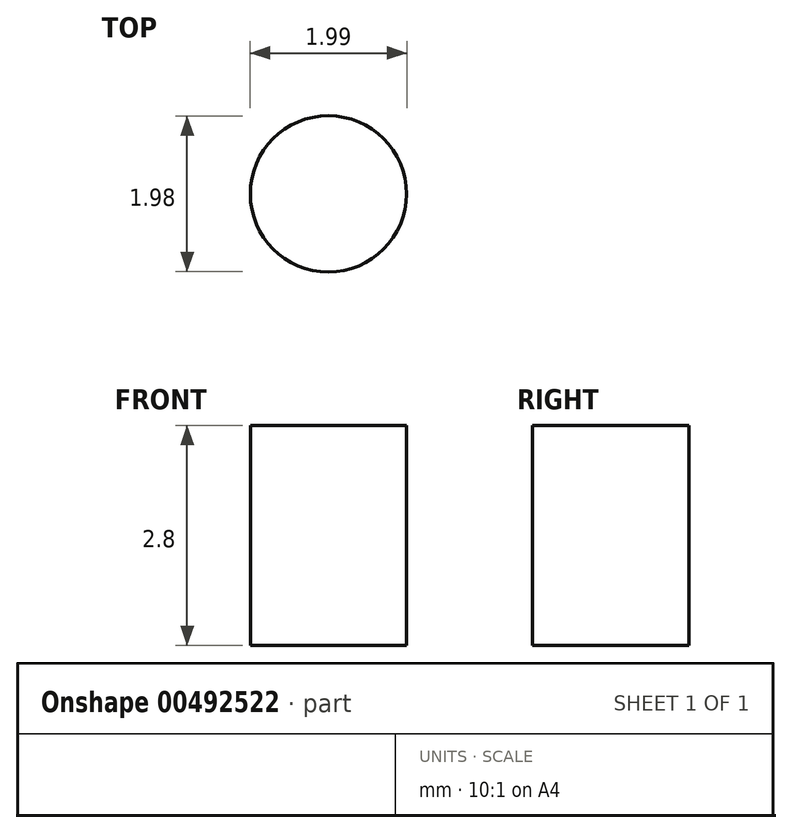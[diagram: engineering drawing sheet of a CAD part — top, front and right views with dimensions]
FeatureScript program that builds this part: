
annotation { "Feature Type Name" : "Feature", "Feature Type Description" : "" }
export const myFeature = defineFeature(function(context is Context, id is Id, definition is map)
    precondition{}
    {
        {
            var Q0;
            Q0=qCreatedBy(makeId("Top.planeOp"),FACE);
            var sketch = newSketch(context, id + "F0", { "sketchPlane" : qUnion([Q0])});
            skCircle(sketch, "E0", {"center": v(-28.23, 11.15) * mm, "radius": 1 * mm});
            skSolve(sketch);
        }
        {
            var Q0;
            Q0=makeQuery(id+"F0.imprint","IMPRINT",FACE,{"disambiguationData":[TD([[makeQuery(id+"F0.imprint","IMPRINT",EDGE,{"derivedFrom":sQuery(id+"F0.wireOp",EDGE,"E0")}),1.0]])]});
            extrude(context, id + "F1", {"entities" : qUnion([Q0]), "depth" : 2.8 * mm});
        }
    });
